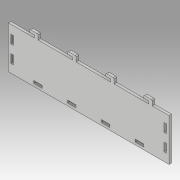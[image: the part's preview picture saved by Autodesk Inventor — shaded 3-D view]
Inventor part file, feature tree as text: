
AUTODESK INVENTOR PART (.ipt)
format: ipt  version: 2019.3 (Build 233278000, 278)  size: 184,320 bytes
history: native  units: mm
features: extrude x1, sketch x1
ambient origin geometry x8: Origin, YZ Plane, XZ Plane, XY Plane, X Axis, Y Axis, Z Axis, Center Point
bodies: Body1 (feature_tree)
feature tree (2):
  extrude  "Extrusion3"  Depth=50.0mm
  sketch  "Sketch1"  dims[d6=190.0mm d7=50.0mm d19=20.0mm d23=10.0mm d24=3.0mm d25=3.0mm d26=4.0mm d27=1.0mm d28=45.0mm d29=45.0mm d30=45.0mm d31=31.0mm d34=3.0mm d35=10.0mm d36=10.0mm d37=3.0mm d51=10.0mm d52=30.0mm d53=30.0mm d54=30.0mm d55=30.0mm d56=3.0mm d57=3.0mm d60=10.0mm d61=3.0mm d62=3.0mm d63=0.0mm]
